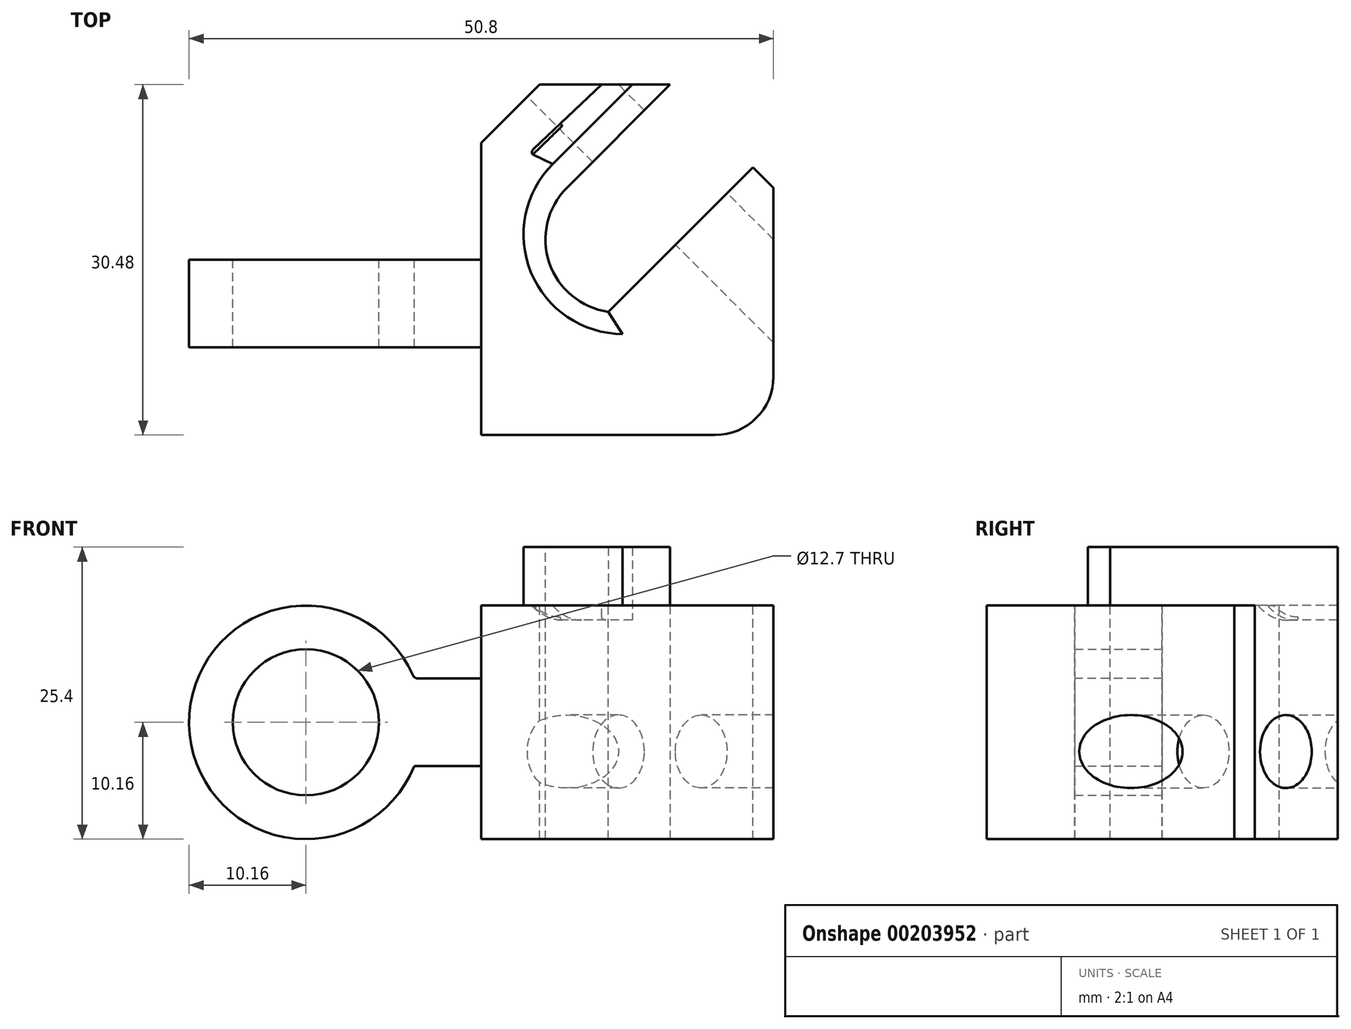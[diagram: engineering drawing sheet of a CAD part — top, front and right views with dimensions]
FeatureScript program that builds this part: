
annotation { "Feature Type Name" : "Feature", "Feature Type Description" : "" }
export const myFeature = defineFeature(function(context is Context, id is Id, definition is map)
    precondition{}
    {
        {
            var Q0;
            Q0=qCreatedBy(makeId("Front.planeOp"),FACE);
            var sketch = newSketch(context, id + "F0", { "sketchPlane" : qUnion([Q0])});
            skCircle(sketch, "E0", {"center": v(0, 0) * mm, "radius": 6.35 * mm});
            skArc(sketch, "E1", {"start": v(9.42, 3.81) * mm, "mid": v(-10.16, 0) * mm, "end": v(9.42, -3.8) * mm});
            skLineSegment(sketch, "E2", {"start": v(0, 0) * mm, "end": v(6.35, 0) * mm});
            skLineSegment(sketch, "E3", {"start": v(15.24, 0) * mm, "end": v(15.24, 3.81) * mm});
            skLineSegment(sketch, "E4", {"start": v(15.24, 3.81) * mm, "end": v(15.24, 0) * mm});
            skLineSegment(sketch, "E5", {"start": v(15.24, 0) * mm, "end": v(15.24, -3.81) * mm});
            skLineSegment(sketch, "E6", {"start": v(15.24, -3.81) * mm, "end": v(9.42, -3.81) * mm});
            skLineSegment(sketch, "E7", {"start": v(15.24, 3.81) * mm, "end": v(9.42, 3.81) * mm});
            skSolve(sketch);
        }
        {
            var Q0;
            Q0 = qSketchRegion(id + "F0", true);
            extrude(context, id + "F1", {"entities" : qUnion([Q0]), "depth" : 7.62 * mm});
        }
        {
            var Q0;
            Q0=makeQuery(id+"F1.opExtrude","SWEPT_FACE",FACE,{"disambiguationData":[OSD([sQuery(id+"F0.wireOp",EDGE,"E4"),sQuery(id+"F0.wireOp",EDGE,"E5")])]});
            var sketch = newSketch(context, id + "F2", { "sketchPlane" : qUnion([Q0])});
            skLineSegment(sketch, "E8", {"start": v(-7.62, 3.81) * mm, "end": v(-15.24, 3.81) * mm});
            skLineSegment(sketch, "E9", {"start": v(-7.62, 3.81) * mm, "end": v(-7.62, 10.16) * mm});
            skLineSegment(sketch, "E10.top", {"start": v(-7.62, 10.16) * mm, "end": v(-15.24, 10.16) * mm});
            skLineSegment(sketch, "E10.right", {"start": v(-15.24, 3.81) * mm, "end": v(-15.24, 10.16) * mm});
            skLineSegment(sketch, "E11", {"start": v(0, 3.81) * mm, "end": v(15.24, 3.81) * mm});
            skLineSegment(sketch, "E12.bottom", {"start": v(-15.24, 10.16) * mm, "end": v(15.24, 10.16) * mm});
            skLineSegment(sketch, "E12.top", {"start": v(-15.24, -10.16) * mm, "end": v(15.24, -10.16) * mm});
            skLineSegment(sketch, "E12.left", {"start": v(-15.24, 10.16) * mm, "end": v(-15.24, -10.16) * mm});
            skLineSegment(sketch, "E12.right", {"start": v(15.24, 10.16) * mm, "end": v(15.24, -10.16) * mm});
            skSolve(sketch);
        }
        {
            var Q0;
            Q0 = qSketchRegion(id + "F2", true);
            extrude(context, id + "F3", {"entities" : qUnion([Q0]), "operationType" : NewBodyOperationType.ADD, "depth" : 25.4 * mm});
        }
        {
            var Q0;
            Q0=makeQuery(id+"F3.opExtrude","SWEPT_FACE",FACE,{"disambiguationData":[OSD([sQuery(id+"F2.wireOp",EDGE,"E12.bottom")])]});
            var sketch = newSketch(context, id + "F4", { "sketchPlane" : qUnion([Q0])});
            skLineSegment(sketch, "E13", {"start": v(40.64, 15.24) * mm, "end": v(31.66, 15.24) * mm});
            skLineSegment(sketch, "E14", {"start": v(40.64, 15.24) * mm, "end": v(40.64, 6.26) * mm});
            skLineSegment(sketch, "E15", {"start": v(31.66, 15.24) * mm, "end": v(40.64, 6.26) * mm});
            skLineSegment(sketch, "E16", {"start": v(31.66, 15.24) * mm, "end": v(22.68, 6.26) * mm});
            skLineSegment(sketch, "E17", {"start": v(40.64, 6.26) * mm, "end": v(31.66, -2.72) * mm});
            skArc(sketch, "E18", {"start": v(22.68, 6.26) * mm, "mid": v(22.68, -2.72) * mm, "end": v(31.66, -2.72) * mm});
            skLineSegment(sketch, "E19", {"start": v(31.66, 15.24) * mm, "end": v(38.62, 22.2) * mm});
            skLineSegment(sketch, "E20", {"start": v(38.62, 22.2) * mm, "end": v(47.59, 13.24) * mm});
            skLineSegment(sketch, "E21", {"start": v(47.59, 13.24) * mm, "end": v(40.64, 6.26) * mm});
            skSolve(sketch);
        }
        {
            var Q0;
            Q0=makeQuery(id+"F4.imprint","IMPRINT",FACE,{"disambiguationData":[TD([[makeQuery(id+"F4.imprint","IMPRINT",EDGE,{"derivedFrom":sQuery(id+"F4.wireOp",EDGE,"E13")}),-1.0]])]});
            var Q1;
            Q1=makeQuery(id+"F4.imprint","IMPRINT",FACE,{"disambiguationData":[TD([[makeQuery(id+"F4.imprint","IMPRINT",EDGE,{"derivedFrom":sQuery(id+"F4.wireOp",EDGE,"E13")}),1.0]])]});
            var Q2;
            Q2=makeQuery(id+"F4.imprint","IMPRINT",FACE,{"disambiguationData":[TD([[makeQuery(id+"F4.imprint","IMPRINT",EDGE,{"derivedFrom":sQuery(id+"F4.wireOp",EDGE,"E15")}),-1.0]])]});
            extrude(context, id + "F5", {"entities" : qUnion([Q0, Q1, Q2]), "operationType" : NewBodyOperationType.REMOVE, "oppositeDirection" : true, "depth" : 25.4 * mm});
        }
        {
            var Q0;
            Q0=makeQuery(id+"F5.boolean.opBoolean","COPY",FACE,{"derivedFrom":makeQuery(id+"F5.opExtrude","SWEPT_FACE",FACE,{"disambiguationData":[OSD([sQuery(id+"F4.wireOp",EDGE,"E16"),sQuery(id+"F4.wireOp",EDGE,"E19")])]})});
            var sketch = newSketch(context, id + "F6", { "sketchPlane" : qUnion([Q0])});
            skLineSegment(sketch, "E22", {"start": v(26.81, 10.16) * mm, "end": v(26.81, -2.54) * mm});
            skPoint(sketch, "E22.endSnap0", {"position": v(26.81, 10.16) * mm});
            skCircle(sketch, "E23", {"center": v(26.81, -2.54) * mm, "radius": 3.18 * mm});
            skSolve(sketch);
        }
        {
            var Q0;
            Q0 = qSketchRegion(id + "F6", true);
            extrude(context, id + "F7", {"entities" : qUnion([Q0]), "operationType" : NewBodyOperationType.REMOVE, "depth" : 127 * mm, "symmetric" : true});
        }
        {
            var Q0;
            Q0=makeQuery(id+"F3.opExtrude","SWEPT_FACE",FACE,{"disambiguationData":[OSD([sQuery(id+"F2.wireOp",EDGE,"E12.bottom")])]});
            var sketch = newSketch(context, id + "F8", { "sketchPlane" : qUnion([Q0])});
            skLineSegment(sketch, "E24", {"start": v(40.64, 6.26) * mm, "end": v(38.84, 8.06) * mm});
            skLineSegment(sketch, "E25", {"start": v(38.84, 8.06) * mm, "end": v(26.27, -4.52) * mm});
            skSolve(sketch);
        }
        {
            var Q0;
            Q0=makeQuery(id+"F8.imprint","IMPRINT",FACE,{"disambiguationData":[TD([[makeQuery(id+"F8.imprint","IMPRINT",EDGE,{"derivedFrom":sQuery(id+"F8.wireOp",EDGE,"E24")}),1.0]])]});
            extrude(context, id + "F9", {"entities" : qUnion([Q0]), "operationType" : NewBodyOperationType.ADD, "oppositeDirection" : true, "depth" : 20.32 * mm});
        }
        {
            var Q0;
            Q0=makeQuery(id+"F5.boolean.opBoolean","COPY",FACE,{"derivedFrom":makeQuery(id+"F5.opExtrude","SWEPT_FACE",FACE,{"disambiguationData":[OSD([sQuery(id+"F4.wireOp",EDGE,"E16"),sQuery(id+"F4.wireOp",EDGE,"E19")])]})});
            var sketch = newSketch(context, id + "F10", { "sketchPlane" : qUnion([Q0])});
            skCircle(sketch, "E26", {"center": v(26.81, -2.54) * mm, "radius": 3.18 * mm});
            skSolve(sketch);
        }
        {
            var Q0;
            Q0=makeQuery(id+"F10.imprint","IMPRINT",FACE,{"disambiguationData":[TD([[makeQuery(id+"F10.imprint","IMPRINT",EDGE,{"derivedFrom":makeQuery(id+"F7.boolean.opBoolean","INTERSECT",EDGE,{"derivedFrom":[makeQuery(id+"F5.boolean.opBoolean","COPY",FACE,{"derivedFrom":makeQuery(id+"F5.opExtrude","SWEPT_FACE",FACE,{"disambiguationData":[OSD([sQuery(id+"F4.wireOp",EDGE,"E16"),sQuery(id+"F4.wireOp",EDGE,"E19")])]})}),makeQuery(id+"F7.opExtrude","SWEPT_FACE",FACE,{"disambiguationData":[OSD([sQuery(id+"F6.wireOp",EDGE,"E23")])]})]})}),-1.0]])]});
            var Q1;
            Q1=sQuery(id+"F10.wireOp",EDGE,"E26");
            extrude(context, id + "F11", {"entities" : qUnion([Q0]), "operationType" : NewBodyOperationType.REMOVE, "surfaceEntities" : qUnion([Q1]), "depth" : 25.4 * mm});
        }
        {
            var Q0;
            Q0=makeQuery(id+"F3.opExtrude","CAP_EDGE",EDGE,{"disambiguationData":[OSD([sQuery(id+"F2.wireOp",EDGE,"E12.left")])],"isStart":false});
            fillet(context, id + "F12", {"entities" : qUnion([Q0]), "radius" : 5.08 * mm, "tangentPropagation" : true, "allowEdgeOverflow" : false});
        }
        {
            var Q0;
            Q0=makeQuery(id+"F1.opExtrude","SWEPT_EDGE",EDGE,{"disambiguationData":[OSD([sQuery(id+"F0.wireOp",EDGE,"E4"),sQuery(id+"F0.wireOp",EDGE,"E7")])]});
            var Q1;
            Q1=makeQuery(id+"F1.opExtrude","SWEPT_EDGE",EDGE,{"disambiguationData":[OSD([sQuery(id+"F0.wireOp",EDGE,"E5"),sQuery(id+"F0.wireOp",EDGE,"E6")])]});
            fillet(context, id + "F13", {"entities" : qUnion([Q0, Q1]), "radius" : 0.5 * mm, "tangentPropagation" : true, "allowEdgeOverflow" : false});
        }
        {
            var Q0;
            Q0=makeQuery(id+"F3.opExtrude","CAP_EDGE",EDGE,{"disambiguationData":[OSD([sQuery(id+"F2.wireOp",EDGE,"E12.right")])],"isStart":true});
            chamfer(context, id + "F14", {"entities" : qUnion([Q0]), "width" : 5.08 * mm, "tangentPropagation" : true});
        }
        {
            var Q0;
            Q0=makeQuery(id+"F9.boolean.opBoolean","MERGE",FACE,{"derivedFrom":[makeQuery(id+"F3.opExtrude","SWEPT_FACE",FACE,{"disambiguationData":[OSD([sQuery(id+"F2.wireOp",EDGE,"E12.bottom")])]}),makeQuery(id+"F9.opExtrude","CAP_FACE",FACE,{"disambiguationData":[OSD([sQuery(id+"F4.wireOp",EDGE,"E17"),sQuery(id+"F4.wireOp",EDGE,"E18"),sQuery(id+"F8.wireOp",EDGE,"E24"),sQuery(id+"F8.wireOp",EDGE,"E25")])],"isStart":true})]});
            var sketch = newSketch(context, id + "F15", { "sketchPlane" : qUnion([Q0])});
            skLineSegment(sketch, "E27", {"start": v(28.36, 15.24) * mm, "end": v(21.45, 8.33) * mm});
            skArc(sketch, "E28", {"start": v(21.45, 8.33) * mm, "mid": v(19.57, -1.09) * mm, "end": v(27.53, -6.46) * mm});
            skLineSegment(sketch, "E29", {"start": v(27.53, -6.46) * mm, "end": v(26.27, -4.52) * mm});
            skLineSegment(sketch, "E30", {"start": v(28.36, 15.24) * mm, "end": v(31.66, 15.24) * mm});
            skLineSegment(sketch, "E31", {"start": v(31.66, 15.24) * mm, "end": v(22.68, 6.26) * mm});
            skArc(sketch, "E32", {"start": v(22.68, 6.26) * mm, "mid": v(21.15, -0.24) * mm, "end": v(26.27, -4.52) * mm});
            skSolve(sketch);
        }
        {
            var Q0;
            Q0 = qSketchRegion(id + "F15", true);
            extrude(context, id + "F16", {"entities" : qUnion([Q0]), "operationType" : NewBodyOperationType.ADD, "depth" : 5.08 * mm});
        }
        {
            var Q0;
            Q0=makeQuery(id+"F9.boolean.opBoolean","MERGE",FACE,{"derivedFrom":[makeQuery(id+"F3.opExtrude","SWEPT_FACE",FACE,{"disambiguationData":[OSD([sQuery(id+"F2.wireOp",EDGE,"E12.bottom")])]}),makeQuery(id+"F9.opExtrude","CAP_FACE",FACE,{"disambiguationData":[OSD([sQuery(id+"F4.wireOp",EDGE,"E17"),sQuery(id+"F4.wireOp",EDGE,"E18"),sQuery(id+"F8.wireOp",EDGE,"E24"),sQuery(id+"F8.wireOp",EDGE,"E25")])],"isStart":true})]});
            var sketch = newSketch(context, id + "F17", { "sketchPlane" : qUnion([Q0])});
            skLineSegment(sketch, "E33", {"start": v(28.36, 15.24) * mm, "end": v(25.72, 15.24) * mm});
            skLineSegment(sketch, "E34", {"start": v(25.72, 15.24) * mm, "end": v(19.42, 9.3) * mm});
            skLineSegment(sketch, "E35", {"start": v(19.42, 9.3) * mm, "end": v(21.45, 8.33) * mm});
            skSolve(sketch);
        }
        {
            var Q0;
            Q0 = qSketchRegion(id + "F17", true);
            var Q1;
            Q1=makeQuery(id+"F17.imprint","IMPRINT",FACE,{"disambiguationData":[TD([[makeQuery(id+"F17.imprint","IMPRINT",EDGE,{"derivedFrom":sQuery(id+"F17.wireOp",EDGE,"E33")}),1.0]])]});
            extrude(context, id + "F18", {"entities" : qUnion([Q0, Q1]), "operationType" : NewBodyOperationType.REMOVE, "oppositeDirection" : true, "depth" : 1.27 * mm});
        }
        {
            var Q0;
            Q0=makeQuery(id+"F18.boolean.opBoolean","COPY",EDGE,{"derivedFrom":makeQuery(id+"F18.opExtrude","CAP_EDGE",EDGE,{"disambiguationData":[OSD([sQuery(id+"F17.wireOp",EDGE,"E35")])],"isStart":false})});
            fillet(context, id + "F19", {"entities" : qUnion([Q0]), "radius" : 5.08 * mm, "tangentPropagation" : true, "allowEdgeOverflow" : false});
        }
        {
            var Q0;
            Q0=makeQuery(id+"F18.boolean.opBoolean","COPY",EDGE,{"derivedFrom":makeQuery(id+"F18.opExtrude","CAP_EDGE",EDGE,{"disambiguationData":[OSD([sQuery(id+"F17.wireOp",EDGE,"E34")])],"isStart":false})});
            fillet(context, id + "F20", {"entities" : qUnion([Q0]), "radius" : 0.25 * mm, "tangentPropagation" : true, "allowEdgeOverflow" : false});
        }
    });
